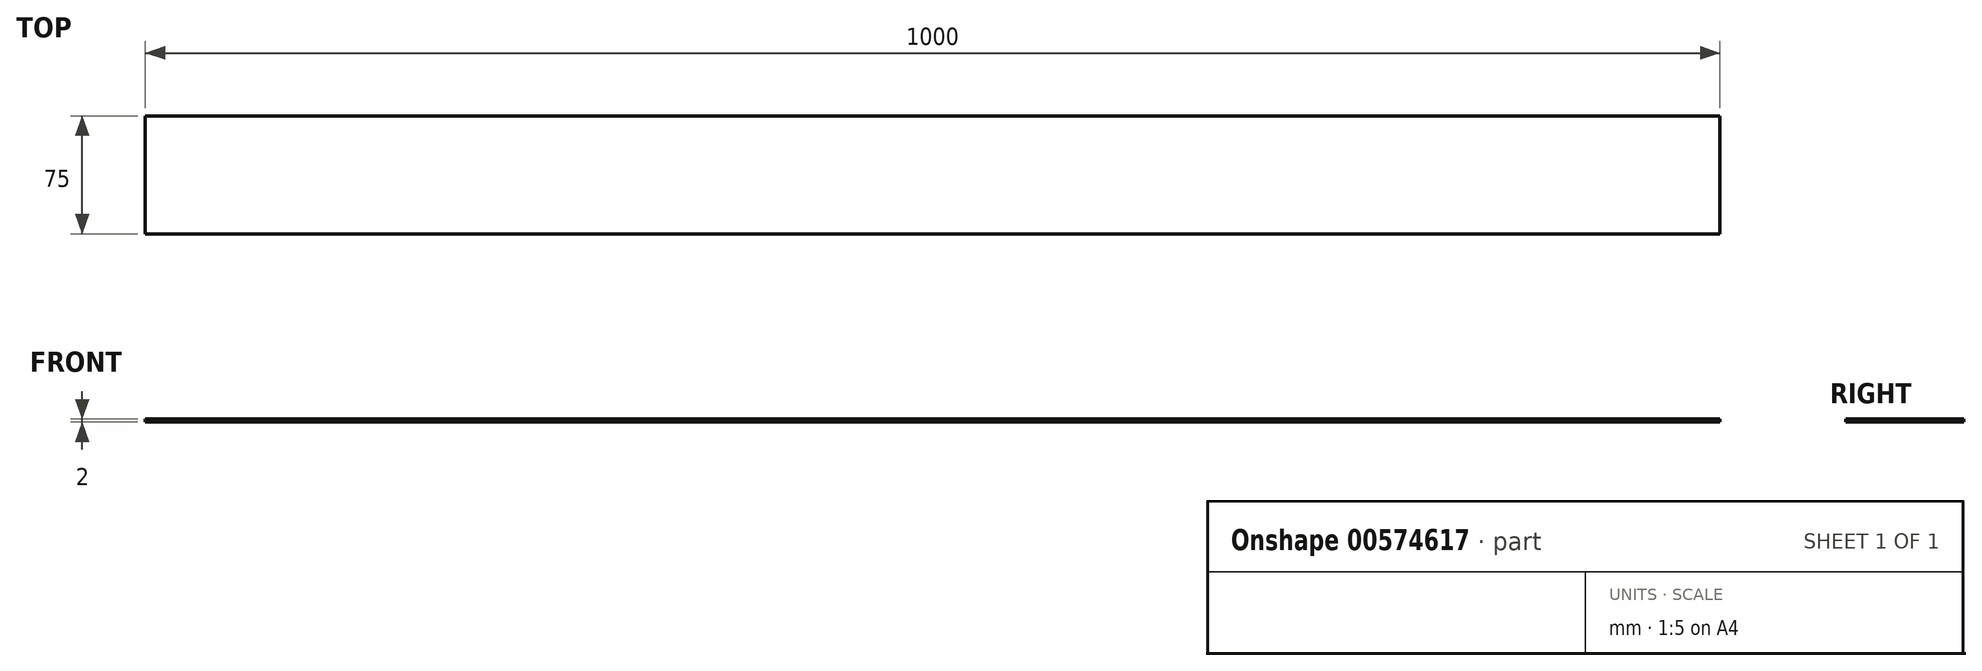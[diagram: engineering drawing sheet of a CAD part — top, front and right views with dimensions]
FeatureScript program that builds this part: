
annotation { "Feature Type Name" : "Feature", "Feature Type Description" : "" }
export const myFeature = defineFeature(function(context is Context, id is Id, definition is map)
    precondition{}
    {
        {
            var Q0;
            Q0=qCreatedBy(makeId("Top.planeOp"),FACE);
            var sketch = newSketch(context, id + "F0", { "sketchPlane" : qUnion([Q0])});
            skLineSegment(sketch, "E0.bottom", {"start": v(0, 0) * mm, "end": v(1000, 0) * mm});
            skLineSegment(sketch, "E0.top", {"start": v(0, 75) * mm, "end": v(1000, 75) * mm});
            skLineSegment(sketch, "E0.left", {"start": v(0, 0) * mm, "end": v(0, 75) * mm});
            skLineSegment(sketch, "E0.right", {"start": v(1000, 0) * mm, "end": v(1000, 75) * mm});
            skSolve(sketch);
        }
        {
            var Q0;
            Q0=makeQuery(id+"F0.imprint","IMPRINT",FACE,{"disambiguationData":[TD([[makeQuery(id+"F0.imprint","IMPRINT",EDGE,{"derivedFrom":sQuery(id+"F0.wireOp",EDGE,"E0.bottom")}),1.0]])]});
            extrude(context, id + "F1", {"entities" : qUnion([Q0]), "depth" : 2 * mm, "offsetDistance" : 25 * mm});
        }
    });
